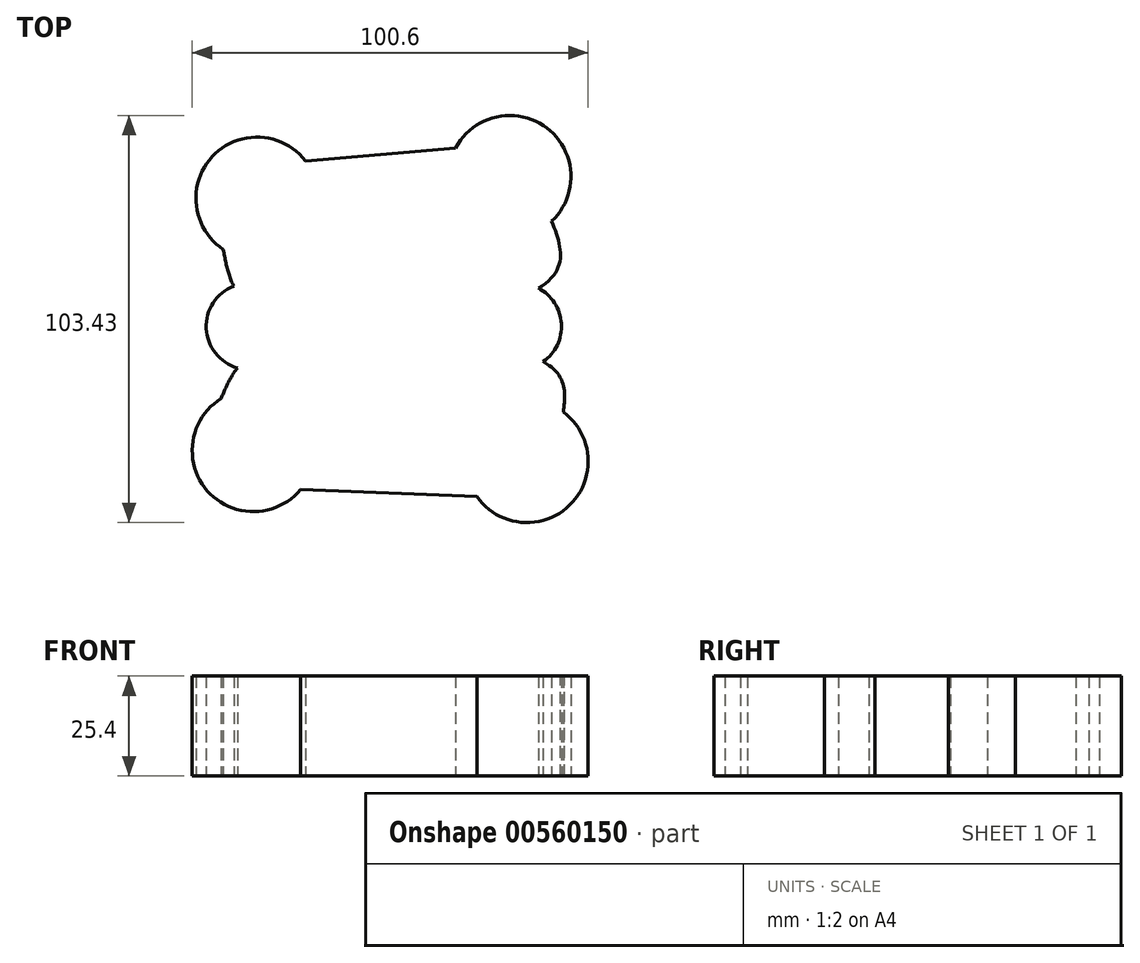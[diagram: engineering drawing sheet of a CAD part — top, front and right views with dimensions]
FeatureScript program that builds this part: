
annotation { "Feature Type Name" : "Feature", "Feature Type Description" : "" }
export const myFeature = defineFeature(function(context is Context, id is Id, definition is map)
    precondition{}
    {
        {
            var Q0;
            Q0=qCreatedBy(makeId("Top.planeOp"),FACE);
            var sketch = newSketch(context, id + "F0", { "sketchPlane" : qUnion([Q0])});
            skArc(sketch, "E0", {"start": v(-22.84, 42.09) * mm, "mid": v(-46.52, 43.12) * mm, "end": v(-43.7, 19.58) * mm});
            skArc(sketch, "E1", {"start": v(39.72, 26.74) * mm, "mid": v(38.5, 50.42) * mm, "end": v(15.33, 45.36) * mm});
            skArc(sketch, "E2", {"start": v(-44.25, -18.3) * mm, "mid": v(-47.77, -41.74) * mm, "end": v(-24.06, -41.4) * mm});
            skArc(sketch, "E3", {"start": v(20.7, -43.18) * mm, "mid": v(44.3, -45.4) * mm, "end": v(42.66, -21.75) * mm});
            skPoint(sketch, "E4.middle", {"position": v(0, 0) * mm});
            skFitSpline(sketch, "E5", {"points": [v(-43.7, 19.58) * mm, v(-39.12, 7.62) * mm, v(-20.95, 0) * mm], "startDerivative": vector(5.23, -29.7) * mm, "endDerivative": vector(39.06, -10.16) * mm});
            skFitSpline(sketch, "E6", {"points": [v(-44.25, -18.3) * mm, v(-38.35, -8.64) * mm, v(-20.95, 0) * mm], "startDerivative": vector(9.94, 23.84) * mm, "endDerivative": vector(35.53, 13.22) * mm});
            skFitSpline(sketch, "E7", {"points": [v(39.72, 26.74) * mm, v(39.72, 12.45) * mm, v(20.95, 0) * mm, v(39.72, -10.41) * mm, v(42.66, -21.75) * mm], "startDerivative": vector(25.4, -66.56) * mm, "endDerivative": vector(-7.17, -59.04) * mm});
            skLineSegment(sketch, "E8", {"start": v(-22.84, 42.09) * mm, "end": v(15.33, 45.36) * mm});
            skLineSegment(sketch, "E9", {"start": v(-24.06, -41.4) * mm, "end": v(20.7, -43.18) * mm});
            skPoint(sketch, "E4.top.end.orphan", {"position": v(-20.95, -24.8) * mm});
            skPoint(sketch, "E10.orphan", {"position": v(20.95, -24.8) * mm});
            skPoint(sketch, "E4.bottom.end.orphan", {"position": v(-20.95, 24.8) * mm});
            skPoint(sketch, "E4.left.start.orphan", {"position": v(20.95, 24.8) * mm});
            skArc(sketch, "E11", {"start": v(-41.03, 10.24) * mm, "mid": v(-48.04, -0.48) * mm, "end": v(-40.13, -10.54) * mm});
            skArc(sketch, "E12", {"start": v(37.57, -8.96) * mm, "mid": v(42.19, 0.74) * mm, "end": v(36.32, 9.72) * mm});
            skSolve(sketch);
        }
        {
            var Q0;
            Q0 = qSketchRegion(id + "F0", true);
            extrude(context, id + "F1", {"entities" : qUnion([Q0]), "depth" : 25.4 * mm, "offsetDistance" : 25.4 * mm});
        }
    });
